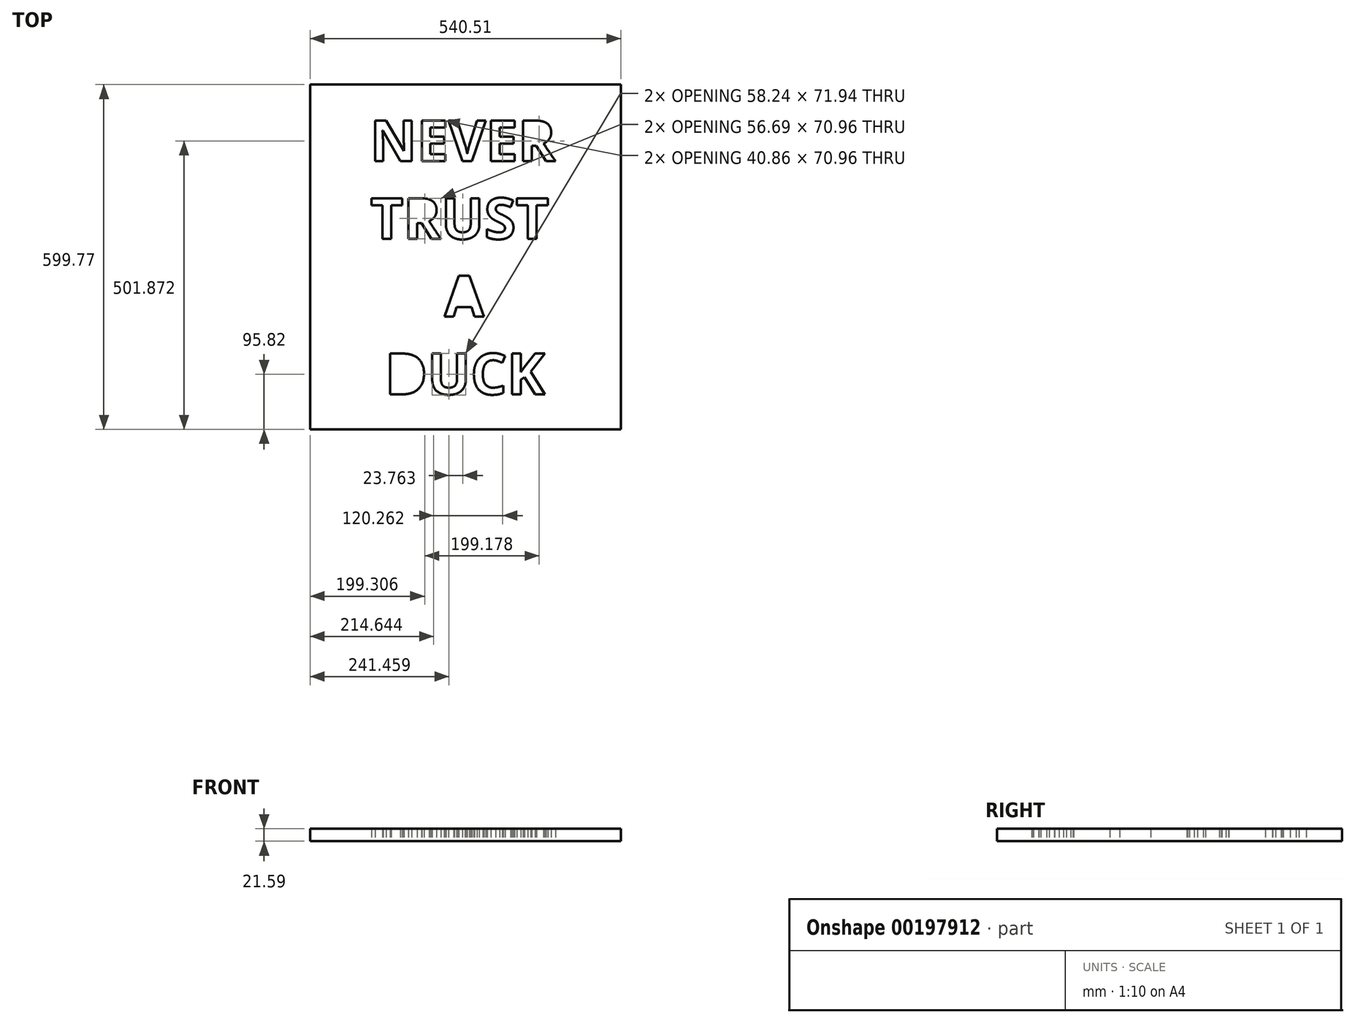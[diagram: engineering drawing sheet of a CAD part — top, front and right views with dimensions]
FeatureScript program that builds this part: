
annotation { "Feature Type Name" : "Feature", "Feature Type Description" : "" }
export const myFeature = defineFeature(function(context is Context, id is Id, definition is map)
    precondition{}
    {
        {
            var Q0;
            Q0=qCreatedBy(makeId("Top.planeOp"),FACE);
            var sketch = newSketch(context, id + "F0", { "sketchPlane" : qUnion([Q0])});
            skText(sketch, "E0", { "text": "NEVER \nTRUST \n     A\n DUCK", "fontName": "OpenSans-Bold.ttf"});
            skLineSegment(sketch, "E1.bottom", {"start": v(-369.99, 186.78) * mm, "end": v(170.52, 186.78) * mm});
            skLineSegment(sketch, "E1.top", {"start": v(-369.99, -413) * mm, "end": v(170.52, -413) * mm});
            skLineSegment(sketch, "E1.left", {"start": v(-369.99, 186.78) * mm, "end": v(-369.99, -413) * mm});
            skLineSegment(sketch, "E1.right", {"start": v(170.52, 186.78) * mm, "end": v(170.52, -413) * mm});
            const initialGuessF0  = {"E0": [-0.26552, 0.0534, 1, 0, 0.07157]};
            skSetInitialGuess(sketch, initialGuessF0);
            skSolve(sketch);
        }
        {
            var Q0;
            Q0 = qSketchRegion(id + "F0", true);
            extrude(context, id + "F1", {"entities" : qUnion([Q0]), "depth" : 21.59 * mm});
        }
    });
